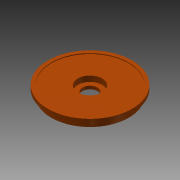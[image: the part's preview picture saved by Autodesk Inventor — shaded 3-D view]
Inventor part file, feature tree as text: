
AUTODESK INVENTOR PART (.ipt)
format: ipt  version: 2015 (Build 190159000, 159)  size: 132,608 bytes
history: native  units: in
note: dims shown in document units (in); Inventor stores cm internally (conversion verified against a paired STEP export)
features: revolve x1, sketch x1
ambient origin geometry x8: Origin, YZ Plane, XZ Plane, XY Plane, X Axis, Y Axis, Z Axis, Center Point
bodies: Body1 (feature_tree)
feature tree (2):
  revolve  "Revolution2"  [1 undecoded]
  sketch  "Sketch1"  dims[d0=2.5935in d1=0.375in d7=0.1in d8=0.088in d9=0.275in d24=0.368in d25=0.207in d26=0.315in d27=0.5in d28=0.207in d30=0.2338in d32=0.25in d33=0.05in d34=1.7637in d35=90.0deg]
note: 1 required parameter value undecoded (feature->parameter linkage not recoverable at this tier; creation-order binding heuristic only, values carry confidence <= 0.55)
